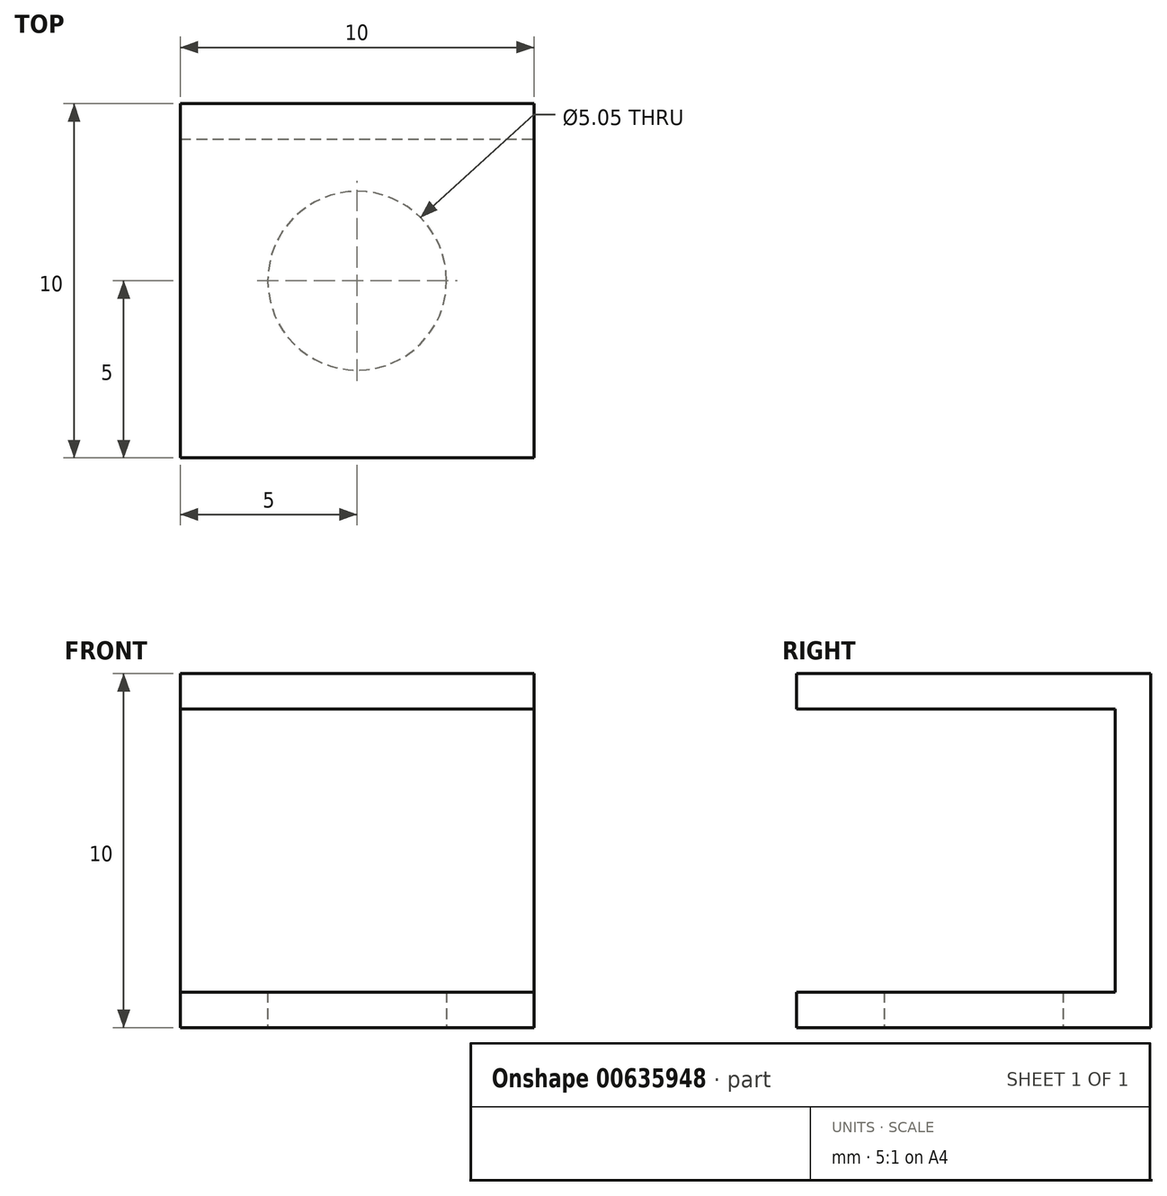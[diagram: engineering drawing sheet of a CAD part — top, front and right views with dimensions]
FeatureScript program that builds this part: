
annotation { "Feature Type Name" : "Feature", "Feature Type Description" : "" }
export const myFeature = defineFeature(function(context is Context, id is Id, definition is map)
    precondition{}
    {
        {
            var Q0;
            Q0=qCreatedBy(makeId("Top.planeOp"),FACE);
            var sketch = newSketch(context, id + "F0", { "sketchPlane" : qUnion([Q0])});
            skLineSegment(sketch, "E0.bottom", {"start": v(5, -5) * mm, "end": v(-5, -5) * mm});
            skLineSegment(sketch, "E0.top", {"start": v(5, 5) * mm, "end": v(-5, 5) * mm});
            skLineSegment(sketch, "E0.left", {"start": v(5, -5) * mm, "end": v(5, 5) * mm});
            skLineSegment(sketch, "E0.right", {"start": v(-5, -5) * mm, "end": v(-5, 5) * mm});
            skPoint(sketch, "E0.middle", {"position": v(0, 0) * mm});
            skCircle(sketch, "E1", {"center": v(0, 0) * mm, "radius": 2.53 * mm});
            skSolve(sketch);
        }
        {
            var Q0;
            Q0=makeQuery(id+"F0.imprint","IMPRINT",FACE,{"disambiguationData":[TD([[makeQuery(id+"F0.imprint","IMPRINT",EDGE,{"derivedFrom":sQuery(id+"F0.wireOp",EDGE,"E0.bottom")}),-1.0]])]});
            extrude(context, id + "F1", {"entities" : qUnion([Q0]), "depth" : 1 * mm, "offsetDistance" : 25 * mm});
        }
        {
            var Q0;
            Q0=makeQuery(id+"F1.opExtrude","CAP_FACE",FACE,{"disambiguationData":[OSD([sQuery(id+"F0.wireOp",EDGE,"E0.bottom"),sQuery(id+"F0.wireOp",EDGE,"E0.top"),sQuery(id+"F0.wireOp",EDGE,"E0.left"),sQuery(id+"F0.wireOp",EDGE,"E0.right"),sQuery(id+"F0.wireOp",EDGE,"E1")])],"isStart":false});
            var sketch = newSketch(context, id + "F2", { "sketchPlane" : qUnion([Q0])});
            skLineSegment(sketch, "E2.bottom", {"start": v(-5, 5) * mm, "end": v(5, 5) * mm});
            skLineSegment(sketch, "E2.top", {"start": v(-5, 4) * mm, "end": v(5, 4) * mm});
            skLineSegment(sketch, "E2.left", {"start": v(-5, 5) * mm, "end": v(-5, 4) * mm});
            skLineSegment(sketch, "E2.right", {"start": v(5, 5) * mm, "end": v(5, 4) * mm});
            skSolve(sketch);
        }
        {
            var Q0;
            Q0 = qSketchRegion(id + "F2", true);
            extrude(context, id + "F3", {"entities" : qUnion([Q0]), "operationType" : NewBodyOperationType.ADD, "depth" : 9 * mm, "offsetDistance" : 25 * mm});
        }
        {
            var Q0;
            Q0=makeQuery(id+"F3.opExtrude","SWEPT_FACE",FACE,{"disambiguationData":[OSD([sQuery(id+"F2.wireOp",EDGE,"E2.top")])]});
            var sketch = newSketch(context, id + "F4", { "sketchPlane" : qUnion([Q0])});
            skLineSegment(sketch, "E3.bottom", {"start": v(-5, 10) * mm, "end": v(5, 10) * mm});
            skLineSegment(sketch, "E3.top", {"start": v(-5, 9) * mm, "end": v(5, 9) * mm});
            skLineSegment(sketch, "E3.left", {"start": v(-5, 10) * mm, "end": v(-5, 9) * mm});
            skLineSegment(sketch, "E3.right", {"start": v(5, 10) * mm, "end": v(5, 9) * mm});
            skSolve(sketch);
        }
        {
            var Q0;
            Q0 = qSketchRegion(id + "F4", true);
            extrude(context, id + "F5", {"entities" : qUnion([Q0]), "operationType" : NewBodyOperationType.ADD, "depth" : 9 * mm, "offsetDistance" : 25 * mm});
        }
    });
